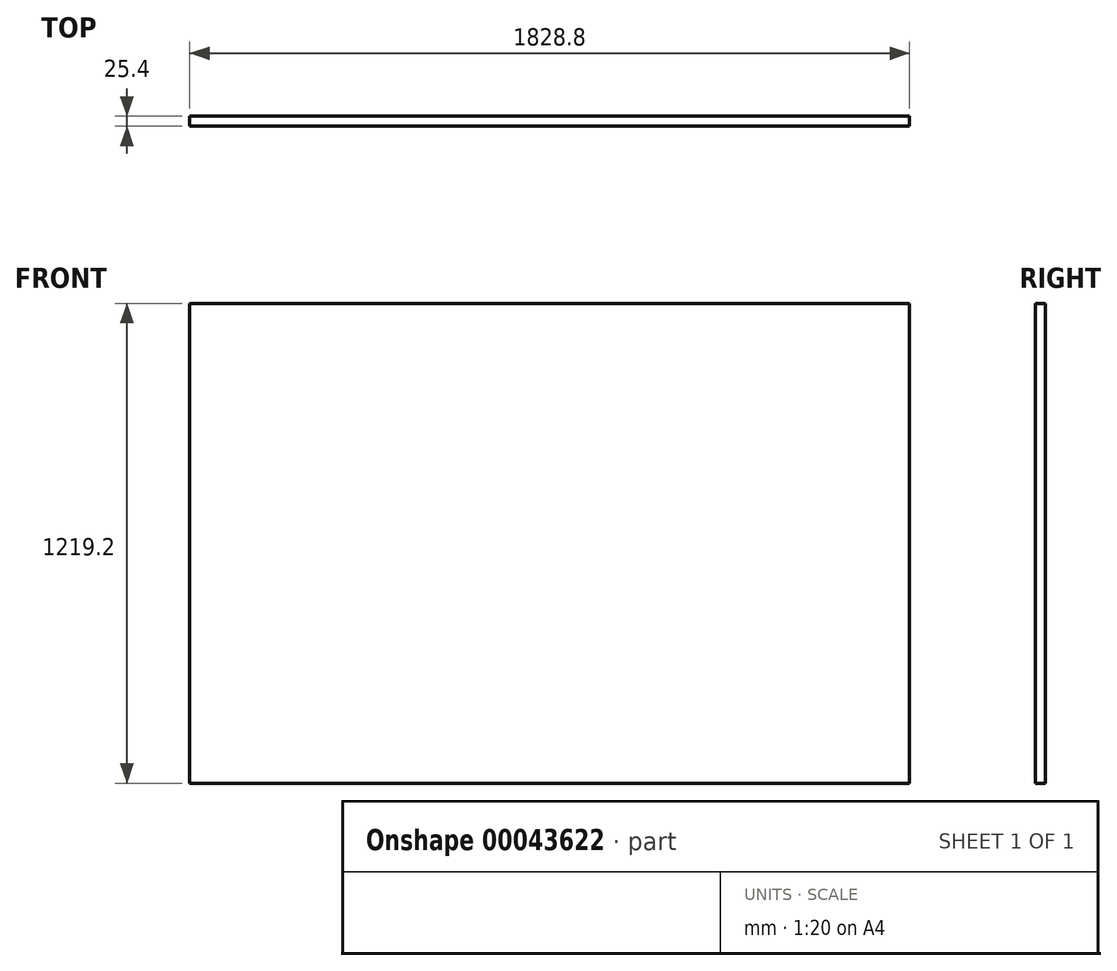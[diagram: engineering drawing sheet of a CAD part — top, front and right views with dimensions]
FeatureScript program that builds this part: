
annotation { "Feature Type Name" : "Feature", "Feature Type Description" : "" }
export const myFeature = defineFeature(function(context is Context, id is Id, definition is map)
    precondition{}
    {
        {
            var Q0;
            Q0=qCreatedBy(makeId("Front.planeOp"),FACE);
            var sketch = newSketch(context, id + "F0", { "sketchPlane" : qUnion([Q0])});
            skLineSegment(sketch, "E0.bottom", {"start": v(-914.4, 609.6) * mm, "end": v(914.4, 609.6) * mm});
            skLineSegment(sketch, "E0.top", {"start": v(-914.4, -609.6) * mm, "end": v(914.4, -609.6) * mm});
            skLineSegment(sketch, "E0.left", {"start": v(-914.4, 609.6) * mm, "end": v(-914.4, -609.6) * mm});
            skLineSegment(sketch, "E0.right", {"start": v(914.4, 609.6) * mm, "end": v(914.4, -609.6) * mm});
            skSolve(sketch);
        }
        {
            var Q0;
            Q0 = qSketchRegion(id + "F0", true);
            extrude(context, id + "F1", {"entities" : qUnion([Q0]), "depth" : 25.4 * mm});
        }
    });
